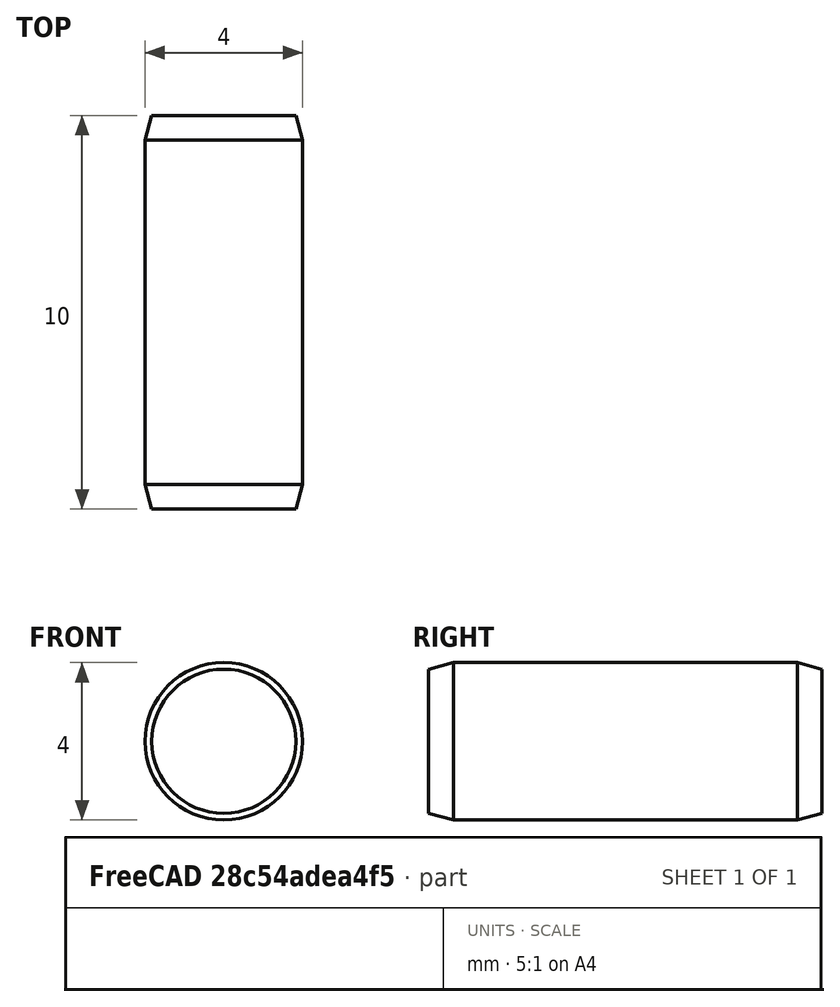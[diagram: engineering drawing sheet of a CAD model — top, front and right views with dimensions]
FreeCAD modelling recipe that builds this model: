
FCSTD DOCUMENT  (FreeCAD 0.15R4470 (Git))
Label: Zyl-Stift_ISO_2338-4x10
License: CC-BY 3.0
LicenseURL: http://creativecommons.org/licenses/by/3.0/
objects: Sketcher::SketchObject×1, PartDesign::Revolution×1
note: 3 computed .brp shape members not serialized (recipe doc carries the construction recipe); baked Part::Feature solids carry a one-line shape summary decoded from their .brp

FEATURE [Sketcher::SketchObject] Sketch
  Placement = pos=(0,0,0) rot=(0.57735,0.57735,0.57735;2.0944rad)
  sketch-geometry (7):
    g0: LineSegment StartX=0 StartY=0 StartZ=0 EndX=0 EndY=1.83119 EndZ=0
    g1: LineSegment StartX=0 StartY=1.83119 StartZ=0 EndX=0.63 EndY=2 EndZ=0
    g2: LineSegment StartX=0.63 StartY=2 StartZ=0 EndX=9.37 EndY=2 EndZ=0
    g3: LineSegment StartX=9.37 StartY=2 StartZ=0 EndX=10 EndY=1.83119 EndZ=0
    g4: LineSegment StartX=10 StartY=1.83119 StartZ=0 EndX=10 EndY=0 EndZ=0
    g5: LineSegment StartX=10 StartY=0 StartZ=0 EndX=0 EndY=0 EndZ=0
    g6: LineSegment [constr] StartX=0 StartY=1.83119 StartZ=0 EndX=10 EndY=1.83119 EndZ=0
  constraints (19):
    c: Coincident(g0,g-1)
    c: PointOnObject(g0,g-2)
    c: Coincident(g0,g1)
    c: Coincident(g1,g2)
    c: Horizontal(g2)
    c: Coincident(g2,g3)
    c: Coincident(g3,g4)
    c: Vertical(g4)
    c: Coincident(g4,g5)
    c: Coincident(g5,g-1)
    c: Horizontal(g5)
    c: Equal(g3,g1)
    c: Coincident(g6,g0)
    c: Coincident(g6,g3)
    c: Horizontal(g6)
    c: Angle(g6,g1) = 0.261799
    c: DistanceY(g-1,g1) = 2
    c: DistanceX(g5) = -10
    c: DistanceX(g1) = 0.63
FEATURE [PartDesign::Revolution] Revolution  label="Zyl-Stift ISO 2338-4x10 #"
  Angle = 360
  Axis = (0,1,0)
  Base = (0,0,0)
  Placement = pos=(0,0,0) rot=(0.57735,0.57735,0.57735;2.0944rad)
  ReferenceAxis = -> Sketch [H_Axis]
  Sketch = -> Sketch
